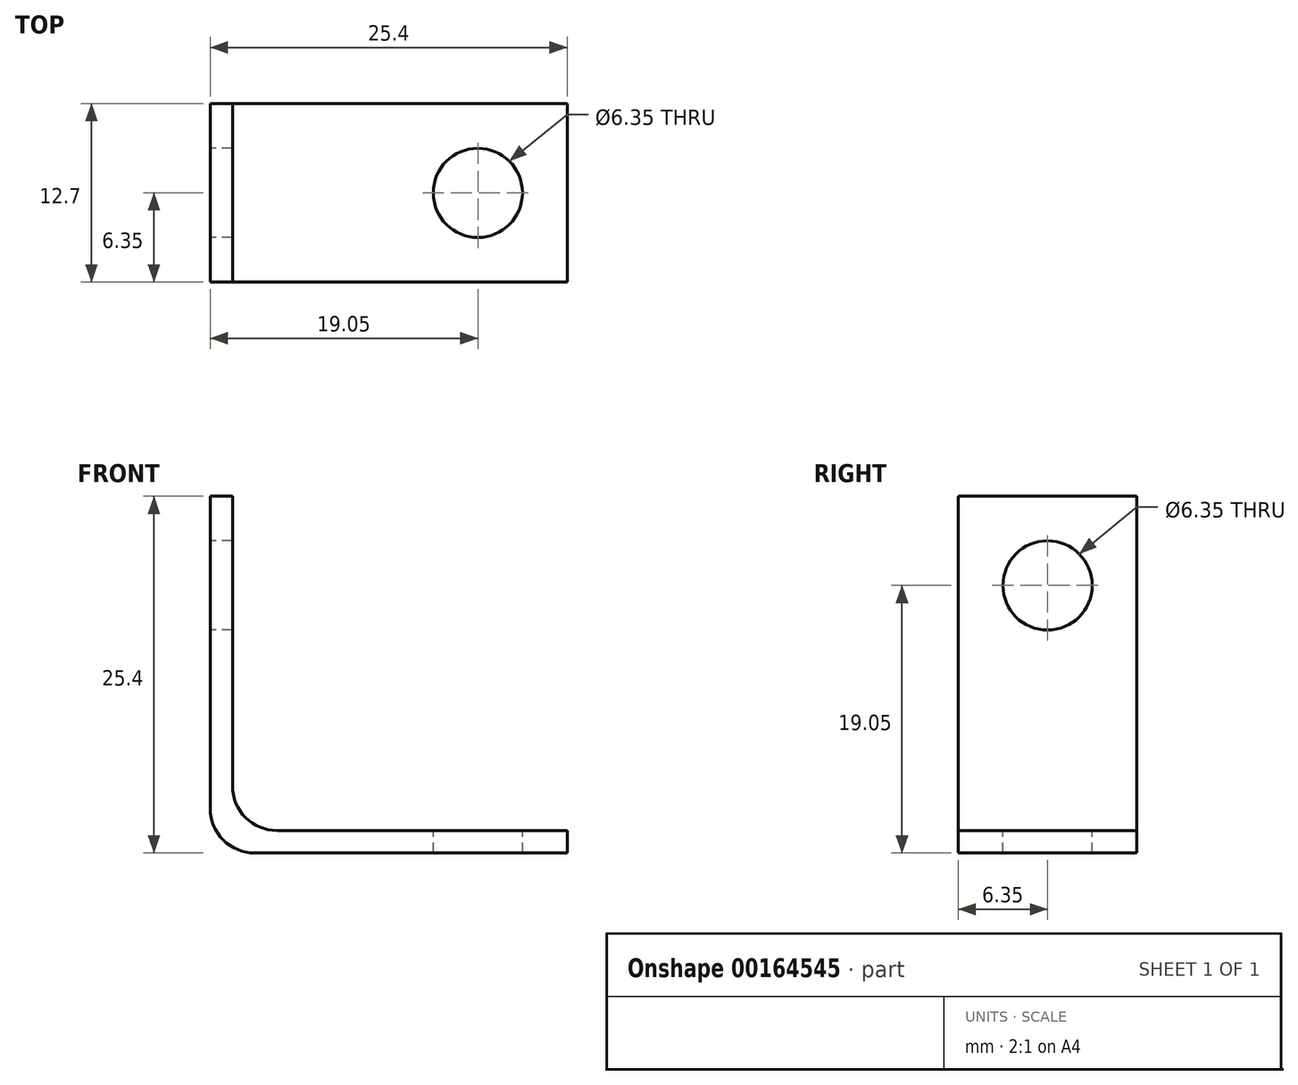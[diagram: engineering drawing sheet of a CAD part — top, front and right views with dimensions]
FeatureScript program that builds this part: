
annotation { "Feature Type Name" : "Feature", "Feature Type Description" : "" }
export const myFeature = defineFeature(function(context is Context, id is Id, definition is map)
    precondition{}
    {
        {
            var Q0;
            Q0=qCreatedBy(makeId("Front.planeOp"),FACE);
            var sketch = newSketch(context, id + "F0", { "sketchPlane" : qUnion([Q0])});
            skLineSegment(sketch, "E0", {"start": v(0, 0) * mm, "end": v(-22.23, 0) * mm});
            skLineSegment(sketch, "E1", {"start": v(-25.4, 3.18) * mm, "end": v(-25.4, 25.4) * mm});
            skLineSegment(sketch, "E2", {"start": v(-25.4, 25.4) * mm, "end": v(-23.81, 25.4) * mm});
            skLineSegment(sketch, "E3", {"start": v(-23.81, 25.4) * mm, "end": v(-23.81, 4.78) * mm});
            skLineSegment(sketch, "E4", {"start": v(-20.64, 1.6) * mm, "end": v(0, 1.6) * mm});
            skLineSegment(sketch, "E5", {"start": v(0, 1.6) * mm, "end": v(0, 0) * mm});
            skPoint(sketch, "E6.visualSharp", {"position": v(-25.4, 0) * mm});
            skArc(sketch, "E6.filletArc", {"start": v(-25.4, 3.18) * mm, "mid": v(-24.47, 0.93) * mm, "end": v(-22.23, 0) * mm});
            skPoint(sketch, "E7.visualSharp", {"position": v(-23.81, 1.6) * mm});
            skArc(sketch, "E7.filletArc", {"start": v(-23.81, 4.78) * mm, "mid": v(-22.88, 2.53) * mm, "end": v(-20.64, 1.6) * mm});
            skSolve(sketch);
        }
        {
            var Q0;
            Q0 = qSketchRegion(id + "F0", true);
            extrude(context, id + "F1", {"entities" : qUnion([Q0]), "endBound" : BoundingType.SYMMETRIC, "depth" : 12.7 * mm});
        }
        {
            var Q0;
            Q0=makeQuery(id+"F1.opExtrude","SWEPT_FACE",FACE,{"disambiguationData":[OSD([sQuery(id+"F0.wireOp",EDGE,"E1")])]});
            var sketch = newSketch(context, id + "F2", { "sketchPlane" : qUnion([Q0])});
            skCircle(sketch, "E8", {"center": v(0, 19.05) * mm, "radius": 3.18 * mm});
            skSolve(sketch);
        }
        {
            var Q0;
            Q0=makeQuery(id+"F2.imprint","IMPRINT",FACE,{"disambiguationData":[TD([[makeQuery(id+"F2.imprint","IMPRINT",EDGE,{"derivedFrom":sQuery(id+"F2.wireOp",EDGE,"E8")}),1.0]])]});
            extrude(context, id + "F3", {"entities" : qUnion([Q0]), "operationType" : NewBodyOperationType.REMOVE, "oppositeDirection" : true, "depth" : 5.08 * mm});
        }
        {
            var Q0;
            Q0=makeQuery(id+"F1.opExtrude","SWEPT_FACE",FACE,{"disambiguationData":[OSD([sQuery(id+"F0.wireOp",EDGE,"E4")])]});
            var sketch = newSketch(context, id + "F4", { "sketchPlane" : qUnion([Q0])});
            skCircle(sketch, "E9", {"center": v(-6.35, 0) * mm, "radius": 3.18 * mm});
            skSolve(sketch);
        }
        {
            var Q0;
            Q0 = qSketchRegion(id + "F4", true);
            extrude(context, id + "F5", {"entities" : qUnion([Q0]), "operationType" : NewBodyOperationType.REMOVE, "oppositeDirection" : true, "depth" : 5.08 * mm});
        }
    });
